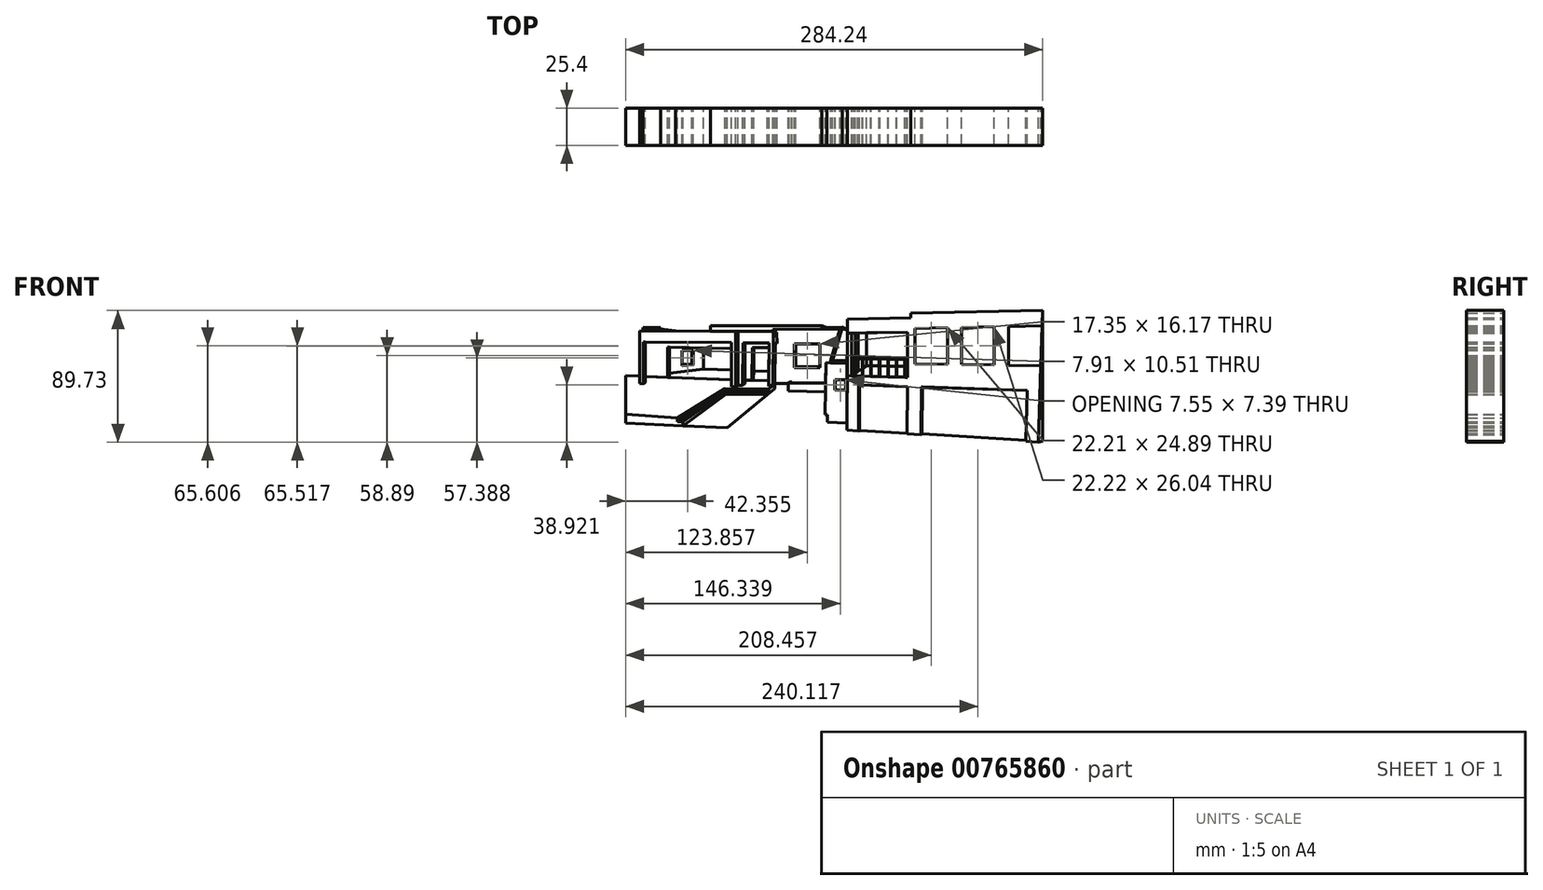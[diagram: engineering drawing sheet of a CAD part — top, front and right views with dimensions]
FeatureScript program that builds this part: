
annotation { "Feature Type Name" : "Feature", "Feature Type Description" : "" }
export const myFeature = defineFeature(function(context is Context, id is Id, definition is map)
    precondition{}
    {
        {
            var Q0;
            Q0=qCreatedBy(makeId("Front.planeOp"),FACE);
            var sketch = newSketch(context, id + "F0", { "sketchPlane" : qUnion([Q0])});
            skSolve(sketch);
        }
        {
            var Q0;
            Q0=qCreatedBy(makeId("Front.planeOp"),FACE);
            var sketch = newSketch(context, id + "F1", { "sketchPlane" : qUnion([Q0])});
            skPoint(sketch, "E0.0", {"position": v(-146.62, 105.14) * mm});
            skPoint(sketch, "E1.0", {"position": v(139.06, 105.14) * mm});
            skPoint(sketch, "E2.0", {"position": v(139.06, -109.12) * mm});
            skPoint(sketch, "E3.0", {"position": v(-146.62, -109.12) * mm});
            skLineSegment(sketch, "E4", {"start": v(-146.62, 105.14) * mm, "end": v(139.06, 105.14) * mm});
            skLineSegment(sketch, "E5", {"start": v(139.06, 105.14) * mm, "end": v(139.06, -109.12) * mm});
            skLineSegment(sketch, "E6", {"start": v(139.06, -109.12) * mm, "end": v(-146.62, -109.12) * mm});
            skLineSegment(sketch, "E7", {"start": v(-146.62, -109.12) * mm, "end": v(-146.62, 105.14) * mm});
            skLineSegment(sketch, "E8", {"start": v(-137.03, 20.59) * mm, "end": v(-48.72, 20.2) * mm});
            skLineSegment(sketch, "E9", {"start": v(-48.8, 12.25) * mm, "end": v(-49.11, -17.1) * mm});
            skLineSegment(sketch, "E10", {"start": v(-48.72, 20.2) * mm, "end": v(-45.8, 20.18) * mm});
            skLineSegment(sketch, "E11", {"start": v(-45.8, 20.18) * mm, "end": v(-43.5, 19.7) * mm});
            skLineSegment(sketch, "E12", {"start": v(-45.8, 20.18) * mm, "end": v(-46.2, -17.22) * mm});
            skLineSegment(sketch, "E13", {"start": v(-43.5, 19.7) * mm, "end": v(-43.41, 12.03) * mm});
            skLineSegment(sketch, "E14", {"start": v(-43.41, 12.03) * mm, "end": v(-44.68, 12.04) * mm});
            skLineSegment(sketch, "E15", {"start": v(-44.68, 12.04) * mm, "end": v(-44.98, -16.42) * mm});
            skLineSegment(sketch, "E16", {"start": v(-44.98, -16.42) * mm, "end": v(-46.2, -17.22) * mm});
            skLineSegment(sketch, "E17", {"start": v(-49.11, -17.1) * mm, "end": v(-46.2, -17.22) * mm});
            skLineSegment(sketch, "E18", {"start": v(-137.03, 20.59) * mm, "end": v(-137.03, -15.42) * mm});
            skLineSegment(sketch, "E19", {"start": v(-134.46, 13.05) * mm, "end": v(-74.47, 12.64) * mm});
            skLineSegment(sketch, "E20", {"start": v(-74.47, 12.64) * mm, "end": v(-74.59, -17.7) * mm});
            skLineSegment(sketch, "E21", {"start": v(-74.59, -17.7) * mm, "end": v(-71.72, -17.7) * mm});
            skLineSegment(sketch, "E22", {"start": v(-48.8, 12.25) * mm, "end": v(-66.56, 12.44) * mm});
            skLineSegment(sketch, "E23", {"start": v(-66.56, 12.44) * mm, "end": v(-66.86, -16.48) * mm});
            skLineSegment(sketch, "E24", {"start": v(-65.22, 12.42) * mm, "end": v(-65.22, -15.22) * mm});
            skLineSegment(sketch, "E25", {"start": v(-71.72, -17.7) * mm, "end": v(-70.05, -16.47) * mm});
            skLineSegment(sketch, "E26", {"start": v(-70.05, -16.47) * mm, "end": v(-66.86, -16.48) * mm});
            skLineSegment(sketch, "E27", {"start": v(-66.86, -16.48) * mm, "end": v(-65.22, -15.22) * mm});
            skLineSegment(sketch, "E28", {"start": v(-70.05, -16.47) * mm, "end": v(-70.05, 20.29) * mm});
            skLineSegment(sketch, "E29", {"start": v(-71.72, -17.7) * mm, "end": v(-71.72, 20.3) * mm});
            skLineSegment(sketch, "E30", {"start": v(-134.46, 13.05) * mm, "end": v(-134.46, -15.51) * mm});
            skLineSegment(sketch, "E31", {"start": v(-117.92, 9.32) * mm, "end": v(-74.49, 8.64) * mm});
            skLineSegment(sketch, "E32", {"start": v(-117.92, 9.32) * mm, "end": v(-117.92, -11.06) * mm});
            skLineSegment(sketch, "E33", {"start": v(-116.53, 9.3) * mm, "end": v(-116.53, -11.1) * mm});
            skLineSegment(sketch, "E34", {"start": v(-74.57, -12.64) * mm, "end": v(-133.04, -10.5) * mm});
            skLineSegment(sketch, "E35", {"start": v(-60.15, 9.2) * mm, "end": v(-48.84, 9.08) * mm});
            skLineSegment(sketch, "E36", {"start": v(-60.15, 9.2) * mm, "end": v(-60.38, -13.22) * mm});
            skLineSegment(sketch, "E37", {"start": v(-60.38, -13.22) * mm, "end": v(-59.39, -12.35) * mm});
            skLineSegment(sketch, "E38", {"start": v(-59.39, -12.35) * mm, "end": v(-59.16, 9.2) * mm});
            skLineSegment(sketch, "E39", {"start": v(-60.38, -13.22) * mm, "end": v(-65.22, -13.17) * mm});
            skLineSegment(sketch, "E40", {"start": v(-134.8, 20.58) * mm, "end": v(-134.8, 22.9) * mm});
            skLineSegment(sketch, "E41", {"start": v(-134.8, 22.9) * mm, "end": v(-122.83, 22.9) * mm});
            skLineSegment(sketch, "E42", {"start": v(-122.83, 22.9) * mm, "end": v(-122.83, 20.52) * mm});
            skLineSegment(sketch, "E43", {"start": v(-122.83, 21.71) * mm, "end": v(-112.4, 20.48) * mm});
            skLineSegment(sketch, "E44", {"start": v(-88.8, 20.37) * mm, "end": v(-88.79, 24.1) * mm});
            skLineSegment(sketch, "E45", {"start": v(-88.79, 24.1) * mm, "end": v(-12.82, 24.1) * mm});
            skLineSegment(sketch, "E46", {"start": v(-12.82, 24.1) * mm, "end": v(-12.82, 21.75) * mm});
            skLineSegment(sketch, "E47", {"start": v(-12.82, 24.1) * mm, "end": v(-9.44, 22.83) * mm});
            skLineSegment(sketch, "E48", {"start": v(-9.44, 22.83) * mm, "end": v(1.15, 22.94) * mm});
            skLineSegment(sketch, "E49", {"start": v(1.15, 22.94) * mm, "end": v(4.61, 21.65) * mm});
            skLineSegment(sketch, "E50", {"start": v(-46.06, 20.18) * mm, "end": v(-46.08, 21.6) * mm});
            skLineSegment(sketch, "E51", {"start": v(-46.08, 21.6) * mm, "end": v(0.68, 21.82) * mm});
            skLineSegment(sketch, "E52", {"start": v(0.68, 21.82) * mm, "end": v(4.6, 21.08) * mm});
            skLineSegment(sketch, "E53", {"start": v(4.65, 28.4) * mm, "end": v(4.27, -47.14) * mm});
            skLineSegment(sketch, "E54", {"start": v(4.65, 28.4) * mm, "end": v(47.74, 29.39) * mm});
            skLineSegment(sketch, "E55", {"start": v(137.62, 34.42) * mm, "end": v(47.67, 32.53) * mm});
            skLineSegment(sketch, "E56", {"start": v(47.74, 29.39) * mm, "end": v(47.67, 32.53) * mm});
            skLineSegment(sketch, "E57", {"start": v(137.62, 34.42) * mm, "end": v(134.95, -55.31) * mm});
            skLineSegment(sketch, "E58.bottom", {"start": v(-31.44, 11.66) * mm, "end": v(-14.09, 11.66) * mm});
            skLineSegment(sketch, "E58.top", {"start": v(-31.44, -4.5) * mm, "end": v(-14.09, -4.5) * mm});
            skLineSegment(sketch, "E58.left", {"start": v(-31.44, 11.66) * mm, "end": v(-31.44, -4.5) * mm});
            skLineSegment(sketch, "E58.right", {"start": v(-14.09, 11.66) * mm, "end": v(-14.09, -4.5) * mm});
            skLineSegment(sketch, "E59", {"start": v(-30.69, 11.66) * mm, "end": v(-30.69, -3.64) * mm});
            skLineSegment(sketch, "E60", {"start": v(-30.69, -3.64) * mm, "end": v(-14.09, -3.89) * mm});
            skLineSegment(sketch, "E61", {"start": v(-31.44, -4.5) * mm, "end": v(-30.69, -3.64) * mm});
            skLineSegment(sketch, "E62", {"start": v(7.63, -10.17) * mm, "end": v(45.5, -11.08) * mm});
            skLineSegment(sketch, "E63", {"start": v(45.5, -11.08) * mm, "end": v(45.65, 19.49) * mm});
            skLineSegment(sketch, "E64", {"start": v(45.65, 19.49) * mm, "end": v(4.6, 18.99) * mm});
            skLineSegment(sketch, "E65", {"start": v(7.63, -10.17) * mm, "end": v(7.63, 19.02) * mm});
            skLineSegment(sketch, "E66", {"start": v(7.63, -10.17) * mm, "end": v(4.45, -10.1) * mm});
            skLineSegment(sketch, "E67", {"start": v(-9.44, 22.83) * mm, "end": v(-9.43, 21.77) * mm});
            skLineSegment(sketch, "E68", {"start": v(1.15, 22.94) * mm, "end": v(1.17, 21.73) * mm});
            skLineSegment(sketch, "E69", {"start": v(0.68, 21.82) * mm, "end": v(0.57, -1.36) * mm});
            skLineSegment(sketch, "E70", {"start": v(-134.46, -15.51) * mm, "end": v(-137.03, -15.42) * mm});
            skLineSegment(sketch, "E71", {"start": v(-134.46, -15.51) * mm, "end": v(-133.04, -14.77) * mm});
            skLineSegment(sketch, "E72", {"start": v(50.73, 22.19) * mm, "end": v(72.94, 22.65) * mm});
            skLineSegment(sketch, "E73", {"start": v(136.5, -3.21) * mm, "end": v(114.66, -2.88) * mm});
            skLineSegment(sketch, "E74", {"start": v(50.73, -1.9) * mm, "end": v(50.73, 22.19) * mm});
            skLineSegment(sketch, "E75", {"start": v(72.94, 22.65) * mm, "end": v(72.94, -2.24) * mm});
            skLineSegment(sketch, "E76", {"start": v(82.38, 22.85) * mm, "end": v(82.38, -2.38) * mm});
            skLineSegment(sketch, "E77", {"start": v(104.6, -2.72) * mm, "end": v(104.6, 23.32) * mm});
            skLineSegment(sketch, "E78", {"start": v(114.66, 23.53) * mm, "end": v(114.66, -2.88) * mm});
            skPoint(sketch, "E79.start.orphan", {"position": v(50.73, 10.14) * mm});
            skLineSegment(sketch, "E80.trimOffspring", {"start": v(82.38, 22.85) * mm, "end": v(104.6, 23.32) * mm});
            skLineSegment(sketch, "E81.trimOffspring", {"start": v(72.94, -2.24) * mm, "end": v(50.73, -1.9) * mm});
            skPoint(sketch, "E82.end.orphan", {"position": v(104.6, 9.69) * mm});
            skPoint(sketch, "E82.start.orphan", {"position": v(82.38, 9.69) * mm});
            skLineSegment(sketch, "E83.trimOffspring", {"start": v(114.66, 23.53) * mm, "end": v(137.3, 24) * mm});
            skPoint(sketch, "E84.start.orphan", {"position": v(114.66, 9.69) * mm});
            skLineSegment(sketch, "E85.trimOffspring", {"start": v(104.6, -2.72) * mm, "end": v(82.38, -2.38) * mm});
            skLineSegment(sketch, "E86", {"start": v(12.4, -16.35) * mm, "end": v(45.5, -17.4) * mm});
            skLineSegment(sketch, "E87", {"start": v(127.33, -20) * mm, "end": v(126.3, -54.77) * mm});
            skLineSegment(sketch, "E88", {"start": v(12.4, -16.35) * mm, "end": v(12.23, -47.64) * mm});
            skLineSegment(sketch, "E89", {"start": v(4.27, -47.14) * mm, "end": v(12.23, -47.64) * mm});
            skLineSegment(sketch, "E90", {"start": v(45.5, -17.4) * mm, "end": v(45.34, -49.7) * mm});
            skLineSegment(sketch, "E91", {"start": v(55.1, -17.7) * mm, "end": v(54.94, -50.31) * mm});
            skLineSegment(sketch, "E92.trimOffspring", {"start": v(55.1, -17.7) * mm, "end": v(127.33, -20) * mm});
            skLineSegment(sketch, "E93", {"start": v(7.63, 2.73) * mm, "end": v(45.57, 2.17) * mm});
            skLineSegment(sketch, "E94", {"start": v(7.63, 1.7) * mm, "end": v(45.56, 1.13) * mm});
            skLineSegment(sketch, "E95", {"start": v(8.88, 1.68) * mm, "end": v(8.88, -10.2) * mm});
            skLineSegment(sketch, "E96", {"start": v(9.36, 1.67) * mm, "end": v(9.36, -10.2) * mm});
            skLineSegment(sketch, "E97.1.0.0", {"start": v(15.16, 1.57) * mm, "end": v(15.16, -10.31) * mm});
            skLineSegment(sketch, "E97.1.0.1", {"start": v(14.69, 1.57) * mm, "end": v(14.69, -10.3) * mm});
            skLineSegment(sketch, "E97.2.0.0", {"start": v(20.97, 1.46) * mm, "end": v(20.97, -10.42) * mm});
            skLineSegment(sketch, "E97.2.0.1", {"start": v(20.49, 1.47) * mm, "end": v(20.49, -10.4) * mm});
            skLineSegment(sketch, "E97.3.0.0", {"start": v(26.77, 1.36) * mm, "end": v(26.77, -10.52) * mm});
            skLineSegment(sketch, "E97.3.0.1", {"start": v(26.29, 1.37) * mm, "end": v(26.29, -10.5) * mm});
            skLineSegment(sketch, "E97.4.0.0", {"start": v(32.57, 1.26) * mm, "end": v(32.57, -10.62) * mm});
            skLineSegment(sketch, "E97.4.0.1", {"start": v(32.1, 1.26) * mm, "end": v(32.1, -10.61) * mm});
            skLineSegment(sketch, "E97.5.0.0", {"start": v(38.37, 1.15) * mm, "end": v(38.37, -10.73) * mm});
            skLineSegment(sketch, "E97.5.0.1", {"start": v(37.9, 1.16) * mm, "end": v(37.9, -10.71) * mm});
            skLineSegment(sketch, "E97.6.0.0", {"start": v(44.17, 1.05) * mm, "end": v(44.17, -10.83) * mm});
            skLineSegment(sketch, "E97.6.0.1", {"start": v(43.7, 1.06) * mm, "end": v(43.7, -10.82) * mm});
            skLineSegment(sketch, "E97.direction1", {"start": v(9.36, -10.2) * mm, "end": v(15.16, -10.31) * mm, "construction": true});
            skLineSegment(sketch, "E98", {"start": v(14.69, 1.57) * mm, "end": v(14.69, 1.6) * mm});
            skLineSegment(sketch, "E99", {"start": v(15.16, 1.57) * mm, "end": v(15.16, 1.58) * mm});
            skLineSegment(sketch, "E100", {"start": v(20.49, 1.47) * mm, "end": v(20.49, 1.5) * mm});
            skLineSegment(sketch, "E101", {"start": v(20.97, 1.46) * mm, "end": v(20.97, 1.5) * mm});
            skLineSegment(sketch, "E102", {"start": v(26.29, 1.37) * mm, "end": v(26.29, 1.42) * mm});
            skLineSegment(sketch, "E103", {"start": v(26.77, 1.36) * mm, "end": v(26.77, 1.41) * mm});
            skLineSegment(sketch, "E104", {"start": v(32.1, 1.26) * mm, "end": v(32.1, 1.33) * mm});
            skLineSegment(sketch, "E105", {"start": v(32.57, 1.26) * mm, "end": v(32.57, 1.33) * mm});
            skLineSegment(sketch, "E106", {"start": v(37.9, 1.16) * mm, "end": v(37.9, 1.25) * mm});
            skLineSegment(sketch, "E107", {"start": v(38.37, 1.15) * mm, "end": v(38.37, 1.24) * mm});
            skLineSegment(sketch, "E108", {"start": v(44.17, 1.05) * mm, "end": v(44.17, 1.15) * mm});
            skLineSegment(sketch, "E109", {"start": v(43.7, 1.06) * mm, "end": v(43.7, 1.16) * mm});
            skLineSegment(sketch, "E110", {"start": v(44.17, -10.83) * mm, "end": v(44.17, -11.05) * mm});
            skLineSegment(sketch, "E111", {"start": v(43.7, -10.82) * mm, "end": v(43.7, -11.04) * mm});
            skLineSegment(sketch, "E112", {"start": v(37.9, -10.71) * mm, "end": v(37.9, -10.9) * mm});
            skLineSegment(sketch, "E113", {"start": v(38.37, -10.73) * mm, "end": v(38.37, -10.91) * mm});
            skLineSegment(sketch, "E114", {"start": v(32.1, -10.61) * mm, "end": v(32.1, -10.76) * mm});
            skLineSegment(sketch, "E115", {"start": v(32.57, -10.62) * mm, "end": v(32.57, -10.77) * mm});
            skLineSegment(sketch, "E116", {"start": v(26.29, -10.5) * mm, "end": v(26.29, -10.62) * mm});
            skLineSegment(sketch, "E117", {"start": v(26.77, -10.52) * mm, "end": v(26.77, -10.63) * mm});
            skLineSegment(sketch, "E118", {"start": v(20.49, -10.4) * mm, "end": v(20.49, -10.48) * mm});
            skLineSegment(sketch, "E119", {"start": v(20.97, -10.42) * mm, "end": v(20.97, -10.49) * mm});
            skLineSegment(sketch, "E120", {"start": v(14.69, -10.3) * mm, "end": v(14.69, -10.34) * mm});
            skLineSegment(sketch, "E121", {"start": v(15.16, -10.31) * mm, "end": v(15.16, -10.35) * mm});
            skLineSegment(sketch, "E122", {"start": v(12.23, -47.64) * mm, "end": v(12.73, -47.24) * mm});
            skLineSegment(sketch, "E123", {"start": v(12.73, -47.24) * mm, "end": v(12.88, -16.37) * mm});
            skLineSegment(sketch, "E124", {"start": v(54.94, -50.31) * mm, "end": v(55.52, -49.75) * mm});
            skLineSegment(sketch, "E125", {"start": v(55.52, -49.75) * mm, "end": v(55.64, -17.73) * mm});
            skLineSegment(sketch, "E126", {"start": v(12.73, -47.24) * mm, "end": v(45.34, -49.28) * mm});
            skLineSegment(sketch, "E127", {"start": v(55.52, -49.75) * mm, "end": v(126.32, -54.18) * mm});
            skLineSegment(sketch, "E128.trimOffspring", {"start": v(126.3, -54.77) * mm, "end": v(134.95, -55.31) * mm});
            skLineSegment(sketch, "E129.trimOffspring", {"start": v(45.34, -49.7) * mm, "end": v(54.94, -50.31) * mm});
            skLineSegment(sketch, "E130", {"start": v(-9.08, -41.6) * mm, "end": v(-9.08, -36.6) * mm});
            skLineSegment(sketch, "E131", {"start": v(-9.08, -36.6) * mm, "end": v(-10.58, -36.6) * mm});
            skLineSegment(sketch, "E132", {"start": v(-10.58, -36.6) * mm, "end": v(-9.86, -1.14) * mm});
            skLineSegment(sketch, "E133", {"start": v(-9.86, -1.14) * mm, "end": v(4.5, -1.44) * mm});
            skLineSegment(sketch, "E134", {"start": v(-4.06, -19.93) * mm, "end": v(-3.9, -12.7) * mm});
            skLineSegment(sketch, "E135", {"start": v(-3.9, -12.7) * mm, "end": v(3.5, -12.85) * mm});
            skLineSegment(sketch, "E136", {"start": v(3.5, -12.85) * mm, "end": v(3.34, -19.93) * mm});
            skLineSegment(sketch, "E137", {"start": v(-4.06, -19.93) * mm, "end": v(3.34, -20.08) * mm});
            skLineSegment(sketch, "E138", {"start": v(3.34, -19.93) * mm, "end": v(3.34, -20.08) * mm});
            skLineSegment(sketch, "E139", {"start": v(-9.08, -41.6) * mm, "end": v(4.3, -42.2) * mm});
            skLineSegment(sketch, "E140", {"start": v(-35.55, -15.05) * mm, "end": v(-10.14, -15.18) * mm});
            skLineSegment(sketch, "E141", {"start": v(-35.55, -15.05) * mm, "end": v(-35.03, -14.37) * mm});
            skLineSegment(sketch, "E142", {"start": v(-33.16, -14.37) * mm, "end": v(-33.57, -14.9) * mm});
            skLineSegment(sketch, "E143", {"start": v(-35.55, -15.05) * mm, "end": v(-35.55, -20.4) * mm});
            skLineSegment(sketch, "E144", {"start": v(-35.55, -20.4) * mm, "end": v(-10.26, -20.9) * mm});
            skLineSegment(sketch, "E145", {"start": v(-44.97, -15.39) * mm, "end": v(-35.55, -15.49) * mm});
            skLineSegment(sketch, "E146", {"start": v(-35.03, -14.37) * mm, "end": v(-33.16, -14.37) * mm});
            skLineSegment(sketch, "E147", {"start": v(-33.57, -14.9) * mm, "end": v(-10.14, -15.02) * mm});
            skLineSegment(sketch, "E148.trimOffspring", {"start": v(15.15, -47.4) * mm, "end": v(15.15, -47.65) * mm});
            skLineSegment(sketch, "E149", {"start": v(-100.3, 7.33) * mm, "end": v(-100.3, -2.64) * mm});
            skLineSegment(sketch, "E150", {"start": v(-100.3, -2.64) * mm, "end": v(-108.22, -3.18) * mm});
            skLineSegment(sketch, "E151", {"start": v(-108.22, -3.18) * mm, "end": v(-108.06, 7.33) * mm});
            skLineSegment(sketch, "E152", {"start": v(-108.06, 7.33) * mm, "end": v(-100.3, 7.33) * mm});
            skLineSegment(sketch, "E153", {"start": v(-101.46, 7.33) * mm, "end": v(-101.46, -2) * mm});
            skLineSegment(sketch, "E154", {"start": v(-101.46, -2) * mm, "end": v(-108.21, -2.47) * mm});
            skLineSegment(sketch, "E155", {"start": v(-101.46, -2) * mm, "end": v(-100.3, -2.64) * mm});
            skLineSegment(sketch, "E156", {"start": v(-116.53, -8.37) * mm, "end": v(-93.36, -5.38) * mm});
            skLineSegment(sketch, "E157", {"start": v(-93.36, -5.38) * mm, "end": v(-93.36, 8.94) * mm});
            skLineSegment(sketch, "E158", {"start": v(-60.38, -13.22) * mm, "end": v(-49.07, -13.33) * mm});
            skLineSegment(sketch, "E159", {"start": v(-133.04, -14.77) * mm, "end": v(-133.04, 13.04) * mm});
            skLineSegment(sketch, "E160", {"start": v(7.63, -1.52) * mm, "end": v(8.88, -1.29) * mm});
            skLineSegment(sketch, "E161", {"start": v(9.9, 19.05) * mm, "end": v(9.9, 3.6) * mm});
            skLineSegment(sketch, "E162", {"start": v(9.9, -7.3) * mm, "end": v(11.96, -7.32) * mm});
            skLineSegment(sketch, "E163", {"start": v(11.96, -7.32) * mm, "end": v(11.96, 1.63) * mm});
            skLineSegment(sketch, "E164.trimOffspring", {"start": v(9.36, -1.2) * mm, "end": v(9.9, -1.1) * mm});
            skLineSegment(sketch, "E165", {"start": v(7.63, -10.17) * mm, "end": v(8.88, -9.3) * mm});
            skLineSegment(sketch, "E166", {"start": v(17.64, -3.23) * mm, "end": v(17.64, 1.55) * mm});
            skLineSegment(sketch, "E167", {"start": v(17.64, -3.23) * mm, "end": v(20.49, -3.27) * mm});
            skLineSegment(sketch, "E168", {"start": v(7.63, -8.47) * mm, "end": v(8.88, -7.82) * mm});
            skLineSegment(sketch, "E169.trimOffspring", {"start": v(9.36, -7.58) * mm, "end": v(9.9, -7.3) * mm});
            skLineSegment(sketch, "E170.trimOffspring", {"start": v(9.36, -8.97) * mm, "end": v(11.74, -7.32) * mm});
            skLineSegment(sketch, "E171.trimOffspring", {"start": v(11.96, -7.17) * mm, "end": v(14.69, -5.28) * mm});
            skLineSegment(sketch, "E172.trimOffspring", {"start": v(15.16, -4.95) * mm, "end": v(17.64, -3.23) * mm});
            skLineSegment(sketch, "E173.trimOffspring", {"start": v(17.64, 2.58) * mm, "end": v(17.64, 19.14) * mm});
            skLineSegment(sketch, "E174.trimOffspring", {"start": v(9.9, 1.66) * mm, "end": v(9.9, -7.3) * mm});
            skLineSegment(sketch, "E175.trimOffspring", {"start": v(11.96, 2.67) * mm, "end": v(11.96, 19.08) * mm});
            skLineSegment(sketch, "E176", {"start": v(-6.8, -1.2) * mm, "end": v(-6.8, 0.37) * mm});
            skLineSegment(sketch, "E177", {"start": v(-6.8, 0.37) * mm, "end": v(4.5, 0.14) * mm});
            skLineSegment(sketch, "E178", {"start": v(-6.8, 0.37) * mm, "end": v(-0.32, 21.81) * mm});
            skLineSegment(sketch, "E179", {"start": v(0.68, 21.82) * mm, "end": v(-5.54, 0.34) * mm});
            skLineSegment(sketch, "E180", {"start": v(7.63, 0.14) * mm, "end": v(8.88, 0.11) * mm});
            skLineSegment(sketch, "E181.trimOffspring", {"start": v(9.36, 0.1) * mm, "end": v(9.9, 0.1) * mm});
            skLineSegment(sketch, "E182.trimOffspring", {"start": v(20.97, -3.28) * mm, "end": v(26.29, -3.36) * mm});
            skLineSegment(sketch, "E183.trimOffspring", {"start": v(26.77, -3.37) * mm, "end": v(32.1, -3.44) * mm});
            skLineSegment(sketch, "E184.trimOffspring", {"start": v(32.57, -3.45) * mm, "end": v(37.9, -3.53) * mm});
            skLineSegment(sketch, "E185.trimOffspring", {"start": v(38.37, -3.54) * mm, "end": v(43.7, -3.62) * mm});
            skLineSegment(sketch, "E186.trimOffspring", {"start": v(44.17, -3.62) * mm, "end": v(45.54, -3.64) * mm});
            skLineSegment(sketch, "E187", {"start": v(-3.6, -12.7) * mm, "end": v(-3.74, -19.7) * mm});
            skLineSegment(sketch, "E188", {"start": v(-3.74, -19.7) * mm, "end": v(3.35, -19.87) * mm});
            skLineSegment(sketch, "E189", {"start": v(-4.06, -19.93) * mm, "end": v(-3.74, -19.7) * mm});
            skLineSegment(sketch, "E190", {"start": v(7.63, 2.73) * mm, "end": v(11.96, 3.6) * mm});
            skLineSegment(sketch, "E191", {"start": v(11.96, 3.6) * mm, "end": v(9.9, 3.6) * mm});
            skLineSegment(sketch, "E192", {"start": v(9.9, 3.6) * mm, "end": v(7.63, 3.15) * mm});
            skLineSegment(sketch, "E193.trimOffspring", {"start": v(9.9, 2.88) * mm, "end": v(9.9, 2.7) * mm});
            skLineSegment(sketch, "E194", {"start": v(11.96, 3.6) * mm, "end": v(11.96, 3.3) * mm});
            skLineSegment(sketch, "E195", {"start": v(11.96, 3.3) * mm, "end": v(9.07, 2.71) * mm});
            skLineSegment(sketch, "E196", {"start": v(-93.36, -5.38) * mm, "end": v(-74.54, -6.07) * mm});
            skLineSegment(sketch, "E197.trimOffspring", {"start": v(-59.33, -6.62) * mm, "end": v(-49, -7) * mm});
            skLineSegment(sketch, "E198", {"start": v(137.62, 34.42) * mm, "end": v(137.62, -54.63) * mm});
            skLineSegment(sketch, "E199", {"start": v(134.95, -55.31) * mm, "end": v(137.62, -54.63) * mm});
            skLineSegment(sketch, "E200", {"start": v(137.62, -54.63) * mm, "end": v(139.06, -54.72) * mm});
            skSolve(sketch);
        }
        {
            var Q0;
            {var subQ7=sQuery(id+"F1.wireOp",EDGE,"E44");Q0=makeQuery(id+"F1.imprint","IMPRINT",FACE,{"disambiguationData":[TD([[makeQuery(id+"F1.imprint","IMPRINT",EDGE,{"derivedFrom":subQ7}),-1.0]])]});}
            extrude(context, id + "F2", {"entities" : qUnion([Q0]), "depth" : 25.4 * mm, "offsetDistance" : 25.4 * mm});
        }
        {
            var Q0;
            {var subQ0=sQuery(id+"F1.wireOp",EDGE,"E46");Q0=makeQuery(id+"F1.imprint","IMPRINT",FACE,{"disambiguationData":[TD([[makeQuery(id+"F1.imprint","IMPRINT",EDGE,{"derivedFrom":subQ0}),1.0]])]});}
            extrude(context, id + "F3", {"entities" : qUnion([Q0]), "depth" : 25.4 * mm, "offsetDistance" : 25.4 * mm});
        }
        {
            var Q0;
            Q0=makeQuery(id+"F1.imprint","IMPRINT",FACE,{"disambiguationData":[TD([[makeQuery(id+"F1.imprint","IMPRINT",EDGE,{"derivedFrom":sQuery(id+"F1.wireOp",EDGE,"E48")}),-1.0]])]});
            extrude(context, id + "F4", {"entities" : qUnion([Q0]), "depth" : 25.4 * mm, "offsetDistance" : 25.4 * mm});
        }
        {
            var Q0;
            {var subQ0=sQuery(id+"F1.wireOp",EDGE,"E49");Q0=makeQuery(id+"F1.imprint","IMPRINT",FACE,{"disambiguationData":[TD([[makeQuery(id+"F1.imprint","IMPRINT",EDGE,{"derivedFrom":subQ0}),-1.0]])]});}
            extrude(context, id + "F5", {"entities" : qUnion([Q0]), "depth" : 25.4 * mm, "offsetDistance" : 25.4 * mm});
        }
        {
            var Q0;
            {var subQ1=sQuery(id+"F1.wireOp",EDGE,"E40");Q0=makeQuery(id+"F1.imprint","IMPRINT",FACE,{"disambiguationData":[TD([[makeQuery(id+"F1.imprint","IMPRINT",EDGE,{"derivedFrom":subQ1}),-1.0]])]});}
            extrude(context, id + "F6", {"entities" : qUnion([Q0]), "depth" : 25.4 * mm, "offsetDistance" : 25.4 * mm});
        }
        {
            var Q0;
            {var subQ3=sQuery(id+"F1.wireOp",EDGE,"E43");Q0=makeQuery(id+"F1.imprint","IMPRINT",FACE,{"disambiguationData":[TD([[makeQuery(id+"F1.imprint","IMPRINT",EDGE,{"derivedFrom":subQ3}),-1.0]])]});}
            extrude(context, id + "F7", {"entities" : qUnion([Q0]), "depth" : 25.4 * mm, "offsetDistance" : 25.4 * mm});
        }
        {
            var Q0;
            {var subQ3=sQuery(id+"F1.wireOp",EDGE,"E32");Q0=makeQuery(id+"F1.imprint","IMPRINT",FACE,{"disambiguationData":[TD([[makeQuery(id+"F1.imprint","IMPRINT",EDGE,{"derivedFrom":subQ3}),-1.0]])]});}
            var Q1;
            {var subQ4=sQuery(id+"F1.wireOp",EDGE,"E36");Q1=makeQuery(id+"F1.imprint","IMPRINT",FACE,{"disambiguationData":[TD([[makeQuery(id+"F1.imprint","IMPRINT",EDGE,{"derivedFrom":subQ4}),-1.0]])]});}
            var Q2;
            {var subQ14=sQuery(id+"F1.wireOp",EDGE,"E11");Q2=makeQuery(id+"F1.imprint","IMPRINT",FACE,{"disambiguationData":[TD([[makeQuery(id+"F1.imprint","IMPRINT",EDGE,{"derivedFrom":subQ14}),1.0]])]});}
            extrude(context, id + "F8", {"entities" : qUnion([Q0, Q1, Q2]), "depth" : 25.4 * mm, "offsetDistance" : 25.4 * mm});
        }
        {
            var Q0;
            {var subQ3=sQuery(id+"F1.wireOp",EDGE,"E18");Q0=makeQuery(id+"F1.imprint","IMPRINT",FACE,{"disambiguationData":[TD([[makeQuery(id+"F1.imprint","IMPRINT",EDGE,{"derivedFrom":subQ3}),1.0]])]});}
            var Q1;
            {var subQ0=sQuery(id+"F1.wireOp",EDGE,"E12");Q1=makeQuery(id+"F1.imprint","IMPRINT",FACE,{"disambiguationData":[TD([[makeQuery(id+"F1.imprint","IMPRINT",EDGE,{"derivedFrom":subQ0}),-1.0]])]});}
            var Q2;
            Q2=makeQuery(id+"F1.imprint","IMPRINT",FACE,{"disambiguationData":[TD([[makeQuery(id+"F1.imprint","IMPRINT",EDGE,{"derivedFrom":sQuery(id+"F1.wireOp",EDGE,"E130")}),-1.0]])]});
            extrude(context, id + "F9", {"entities" : qUnion([Q0, Q1, Q2]), "depth" : 25.4 * mm, "offsetDistance" : 25.4 * mm});
        }
        {
            var Q0;
            {var subQ24=sQuery(id+"F1.wireOp",EDGE,"E54");Q0=makeQuery(id+"F1.imprint","IMPRINT",FACE,{"disambiguationData":[TD([[makeQuery(id+"F1.imprint","IMPRINT",EDGE,{"derivedFrom":subQ24}),-1.0]])]});}
            extrude(context, id + "F10", {"entities" : qUnion([Q0]), "depth" : 25.4 * mm, "offsetDistance" : 25.4 * mm});
        }
        {
            var Q0;
            {var subQ4=sQuery(id+"F1.wireOp",EDGE,"E125");Q0=makeQuery(id+"F1.imprint","IMPRINT",FACE,{"disambiguationData":[TD([[makeQuery(id+"F1.imprint","IMPRINT",EDGE,{"derivedFrom":subQ4}),-1.0]])]});}
            var Q1;
            {var subQ1=sQuery(id+"F1.wireOp",EDGE,"E123");Q1=makeQuery(id+"F1.imprint","IMPRINT",FACE,{"disambiguationData":[TD([[makeQuery(id+"F1.imprint","IMPRINT",EDGE,{"derivedFrom":subQ1}),-1.0]])]});}
            extrude(context, id + "F11", {"entities" : qUnion([Q0, Q1]), "depth" : 25.4 * mm, "offsetDistance" : 25.4 * mm});
        }
        {
            var Q0;
            {var subQ4=sQuery(id+"F1.wireOp",EDGE,"E153");Q0=makeQuery(id+"F1.imprint","IMPRINT",FACE,{"disambiguationData":[TD([[makeQuery(id+"F1.imprint","IMPRINT",EDGE,{"derivedFrom":subQ4}),-1.0]])]});}
            var Q1;
            {var subQ3=sQuery(id+"F1.wireOp",EDGE,"E187");Q1=makeQuery(id+"F1.imprint","IMPRINT",FACE,{"disambiguationData":[TD([[makeQuery(id+"F1.imprint","IMPRINT",EDGE,{"derivedFrom":subQ3}),1.0]])]});}
            var Q2;
            {var subQ3=sQuery(id+"F1.wireOp",EDGE,"E59");Q2=makeQuery(id+"F1.imprint","IMPRINT",FACE,{"disambiguationData":[TD([[makeQuery(id+"F1.imprint","IMPRINT",EDGE,{"derivedFrom":subQ3}),1.0]])]});}
            var Q3;
            Q3=makeQuery(id+"F1.imprint","IMPRINT",FACE,{"disambiguationData":[TD([[makeQuery(id+"F1.imprint","IMPRINT",EDGE,{"derivedFrom":sQuery(id+"F1.wireOp",EDGE,"E72")}),-1.0]])]});
            var Q4;
            Q4=makeQuery(id+"F1.imprint","IMPRINT",FACE,{"disambiguationData":[TD([[makeQuery(id+"F1.imprint","IMPRINT",EDGE,{"derivedFrom":sQuery(id+"F1.wireOp",EDGE,"E76")}),1.0]])]});
            var Q5;
            {var subQ0=sQuery(id+"F1.wireOp",EDGE,"E73");Q5=makeQuery(id+"F1.imprint","IMPRINT",FACE,{"disambiguationData":[TD([[makeQuery(id+"F1.imprint","IMPRINT",EDGE,{"derivedFrom":subQ0}),-1.0]])]});}
            extrude(context, id + "F12", {"entities" : qUnion([Q0, Q1, Q2, Q3, Q4, Q5]), "depth" : 25.4 * mm, "offsetDistance" : 25.4 * mm});
        }
        {
            var Q0;
            {var subQ5=sQuery(id+"F1.wireOp",EDGE,"E66");Q0=makeQuery(id+"F1.imprint","IMPRINT",FACE,{"disambiguationData":[TD([[makeQuery(id+"F1.imprint","IMPRINT",EDGE,{"derivedFrom":subQ5}),-1.0]])]});}
            extrude(context, id + "F13", {"entities" : qUnion([Q0]), "depth" : 25.4 * mm, "offsetDistance" : 25.4 * mm});
        }
        {
            var Q0;
            {var subQ0=sQuery(id+"F1.wireOp",EDGE,"E161");Q0=makeQuery(id+"F1.imprint","IMPRINT",FACE,{"disambiguationData":[TD([[makeQuery(id+"F1.imprint","IMPRINT",EDGE,{"derivedFrom":subQ0}),1.0]])]});}
            var Q1;
            {var subQ0=sQuery(id+"F1.wireOp",EDGE,"E163");var subQ7=sQuery(id+"F1.wireOp",EDGE,"E94");var subQ8=makeQuery(id+"F1.imprint","INTERSECT",VERTEX,{"derivedFrom":[subQ7,subQ0]});Q1=makeQuery(id+"F1.imprint","IMPRINT",FACE,{"disambiguationData":[TD([[makeQuery(id+"F1.imprint","IMPRINT",EDGE,{"disambiguationData":[TD([[subQ8,1.0]])],"derivedFrom":subQ7}),-1.0]])]});}
            extrude(context, id + "F14", {"entities" : qUnion([Q0, Q1]), "depth" : 25.4 * mm, "offsetDistance" : 25.4 * mm});
        }
        {
            var Q0;
            {var subQ6=sQuery(id+"F1.wireOp",EDGE,"E93");var subQ21=sQuery(id+"F1.wireOp",EDGE,"E63");var subQ22=makeQuery(id+"F1.imprint","INTERSECT",VERTEX,{"derivedFrom":[subQ21,subQ6]});Q0=makeQuery(id+"F1.imprint","IMPRINT",FACE,{"disambiguationData":[TD([[makeQuery(id+"F1.imprint","IMPRINT",EDGE,{"disambiguationData":[TD([[subQ22,1.0]])],"derivedFrom":subQ21}),1.0]])]});}
            var Q1;
            {var subQ6=sQuery(id+"F1.wireOp",EDGE,"E98");Q1=makeQuery(id+"F1.imprint","IMPRINT",FACE,{"disambiguationData":[TD([[makeQuery(id+"F1.imprint","IMPRINT",EDGE,{"derivedFrom":subQ6}),-1.0]])]});}
            var Q2;
            {var subQ4=sQuery(id+"F1.wireOp",EDGE,"E95");var subQ8=sQuery(id+"F1.wireOp",EDGE,"E62");var subQ9=makeQuery(id+"F1.imprint","INTERSECT",VERTEX,{"derivedFrom":[subQ8,subQ4]});Q2=makeQuery(id+"F1.imprint","IMPRINT",FACE,{"disambiguationData":[TD([[makeQuery(id+"F1.imprint","IMPRINT",EDGE,{"disambiguationData":[TD([[subQ9,-1.0]])],"derivedFrom":subQ8}),1.0]])]});}
            var Q3;
            {var subQ4=sQuery(id+"F1.wireOp",EDGE,"E100");Q3=makeQuery(id+"F1.imprint","IMPRINT",FACE,{"disambiguationData":[TD([[makeQuery(id+"F1.imprint","IMPRINT",EDGE,{"derivedFrom":subQ4}),-1.0]])]});}
            var Q4;
            {var subQ5=sQuery(id+"F1.wireOp",EDGE,"E102");Q4=makeQuery(id+"F1.imprint","IMPRINT",FACE,{"disambiguationData":[TD([[makeQuery(id+"F1.imprint","IMPRINT",EDGE,{"derivedFrom":subQ5}),-1.0]])]});}
            var Q5;
            {var subQ3=sQuery(id+"F1.wireOp",EDGE,"E104");Q5=makeQuery(id+"F1.imprint","IMPRINT",FACE,{"disambiguationData":[TD([[makeQuery(id+"F1.imprint","IMPRINT",EDGE,{"derivedFrom":subQ3}),-1.0]])]});}
            var Q6;
            {var subQ5=sQuery(id+"F1.wireOp",EDGE,"E106");Q6=makeQuery(id+"F1.imprint","IMPRINT",FACE,{"disambiguationData":[TD([[makeQuery(id+"F1.imprint","IMPRINT",EDGE,{"derivedFrom":subQ5}),-1.0]])]});}
            var Q7;
            {var subQ3=sQuery(id+"F1.wireOp",EDGE,"E108");Q7=makeQuery(id+"F1.imprint","IMPRINT",FACE,{"disambiguationData":[TD([[makeQuery(id+"F1.imprint","IMPRINT",EDGE,{"derivedFrom":subQ3}),1.0]])]});}
            extrude(context, id + "F15", {"entities" : qUnion([Q0, Q1, Q2, Q3, Q4, Q5, Q6, Q7]), "depth" : 25.4 * mm, "offsetDistance" : 25.4 * mm});
        }
        {
            var Q0;
            {var subQ5=sQuery(id+"F1.wireOp",EDGE,"E173.trimOffspring");Q0=makeQuery(id+"F1.imprint","IMPRINT",FACE,{"disambiguationData":[TD([[makeQuery(id+"F1.imprint","IMPRINT",EDGE,{"derivedFrom":subQ5}),-1.0]])]});}
            var Q1;
            {var subQ1=sQuery(id+"F1.wireOp",EDGE,"E100");Q1=makeQuery(id+"F1.imprint","IMPRINT",FACE,{"disambiguationData":[TD([[makeQuery(id+"F1.imprint","IMPRINT",EDGE,{"derivedFrom":subQ1}),1.0]])]});}
            var Q2;
            {var subQ0=sQuery(id+"F1.wireOp",EDGE,"E101");Q2=makeQuery(id+"F1.imprint","IMPRINT",FACE,{"disambiguationData":[TD([[makeQuery(id+"F1.imprint","IMPRINT",EDGE,{"derivedFrom":subQ0}),-1.0]])]});}
            var Q3;
            {var subQ0=sQuery(id+"F1.wireOp",EDGE,"E103");Q3=makeQuery(id+"F1.imprint","IMPRINT",FACE,{"disambiguationData":[TD([[makeQuery(id+"F1.imprint","IMPRINT",EDGE,{"derivedFrom":subQ0}),-1.0]])]});}
            var Q4;
            {var subQ0=sQuery(id+"F1.wireOp",EDGE,"E105");Q4=makeQuery(id+"F1.imprint","IMPRINT",FACE,{"disambiguationData":[TD([[makeQuery(id+"F1.imprint","IMPRINT",EDGE,{"derivedFrom":subQ0}),-1.0]])]});}
            var Q5;
            {var subQ0=sQuery(id+"F1.wireOp",EDGE,"E107");Q5=makeQuery(id+"F1.imprint","IMPRINT",FACE,{"disambiguationData":[TD([[makeQuery(id+"F1.imprint","IMPRINT",EDGE,{"derivedFrom":subQ0}),-1.0]])]});}
            var Q6;
            {var subQ0=sQuery(id+"F1.wireOp",EDGE,"E108");Q6=makeQuery(id+"F1.imprint","IMPRINT",FACE,{"disambiguationData":[TD([[makeQuery(id+"F1.imprint","IMPRINT",EDGE,{"derivedFrom":subQ0}),-1.0]])]});}
            var Q7;
            {var subQ4=sQuery(id+"F1.wireOp",EDGE,"E157");Q7=makeQuery(id+"F1.imprint","IMPRINT",FACE,{"disambiguationData":[TD([[makeQuery(id+"F1.imprint","IMPRINT",EDGE,{"derivedFrom":subQ4}),-1.0]])]});}
            extrude(context, id + "F16", {"entities" : qUnion([Q0, Q1, Q2, Q3, Q4, Q5, Q6, Q7]), "depth" : 25.4 * mm, "offsetDistance" : 25.4 * mm});
        }
        {
            var Q0;
            {var subQ0=sQuery(id+"F1.wireOp",EDGE,"E173.trimOffspring");Q0=makeQuery(id+"F1.imprint","IMPRINT",FACE,{"disambiguationData":[TD([[makeQuery(id+"F1.imprint","IMPRINT",EDGE,{"derivedFrom":subQ0}),1.0]])]});}
            var Q1;
            {var subQ4=sQuery(id+"F1.wireOp",EDGE,"E98");Q1=makeQuery(id+"F1.imprint","IMPRINT",FACE,{"disambiguationData":[TD([[makeQuery(id+"F1.imprint","IMPRINT",EDGE,{"derivedFrom":subQ4}),1.0]])]});}
            var Q2;
            {var subQ1=sQuery(id+"F1.wireOp",EDGE,"E99");Q2=makeQuery(id+"F1.imprint","IMPRINT",FACE,{"disambiguationData":[TD([[makeQuery(id+"F1.imprint","IMPRINT",EDGE,{"derivedFrom":subQ1}),-1.0]])]});}
            var Q3;
            {var subQ1=sQuery(id+"F1.wireOp",EDGE,"E149");Q3=makeQuery(id+"F1.imprint","IMPRINT",FACE,{"disambiguationData":[TD([[makeQuery(id+"F1.imprint","IMPRINT",EDGE,{"derivedFrom":subQ1}),1.0]])]});}
            extrude(context, id + "F17", {"entities" : qUnion([Q0, Q1, Q2, Q3]), "depth" : 25.4 * mm, "offsetDistance" : 25.4 * mm});
        }
        {
            var Q0;
            {var subQ0=sQuery(id+"F1.wireOp",EDGE,"E120");Q0=makeQuery(id+"F1.imprint","IMPRINT",FACE,{"disambiguationData":[TD([[makeQuery(id+"F1.imprint","IMPRINT",EDGE,{"derivedFrom":subQ0}),-1.0]])]});}
            var Q1;
            {var subQ0=sQuery(id+"F1.wireOp",EDGE,"E118");Q1=makeQuery(id+"F1.imprint","IMPRINT",FACE,{"disambiguationData":[TD([[makeQuery(id+"F1.imprint","IMPRINT",EDGE,{"derivedFrom":subQ0}),-1.0]])]});}
            var Q2;
            {var subQ0=sQuery(id+"F1.wireOp",EDGE,"E116");Q2=makeQuery(id+"F1.imprint","IMPRINT",FACE,{"disambiguationData":[TD([[makeQuery(id+"F1.imprint","IMPRINT",EDGE,{"derivedFrom":subQ0}),-1.0]])]});}
            var Q3;
            {var subQ3=sQuery(id+"F1.wireOp",EDGE,"E114");Q3=makeQuery(id+"F1.imprint","IMPRINT",FACE,{"disambiguationData":[TD([[makeQuery(id+"F1.imprint","IMPRINT",EDGE,{"derivedFrom":subQ3}),-1.0]])]});}
            var Q4;
            {var subQ0=sQuery(id+"F1.wireOp",EDGE,"E112");Q4=makeQuery(id+"F1.imprint","IMPRINT",FACE,{"disambiguationData":[TD([[makeQuery(id+"F1.imprint","IMPRINT",EDGE,{"derivedFrom":subQ0}),-1.0]])]});}
            var Q5;
            {var subQ0=sQuery(id+"F1.wireOp",EDGE,"E111");Q5=makeQuery(id+"F1.imprint","IMPRINT",FACE,{"disambiguationData":[TD([[makeQuery(id+"F1.imprint","IMPRINT",EDGE,{"derivedFrom":subQ0}),-1.0]])]});}
            var Q6;
            {var subQ4=sQuery(id+"F1.wireOp",EDGE,"E110");Q6=makeQuery(id+"F1.imprint","IMPRINT",FACE,{"disambiguationData":[TD([[makeQuery(id+"F1.imprint","IMPRINT",EDGE,{"derivedFrom":subQ4}),1.0]])]});}
            extrude(context, id + "F18", {"entities" : qUnion([Q0, Q1, Q2, Q3, Q4, Q5, Q6]), "depth" : 25.4 * mm, "offsetDistance" : 25.4 * mm});
        }
        {
            var Q0;
            {var subQ3=sQuery(id+"F1.wireOp",EDGE,"E197.trimOffspring");Q0=makeQuery(id+"F1.imprint","IMPRINT",FACE,{"disambiguationData":[TD([[makeQuery(id+"F1.imprint","IMPRINT",EDGE,{"derivedFrom":subQ3}),1.0]])]});}
            extrude(context, id + "F19", {"entities" : qUnion([Q0]), "depth" : 25.4 * mm, "offsetDistance" : 25.4 * mm});
        }
        {
            var Q0;
            {var subQ0=sQuery(id+"F1.wireOp",EDGE,"E156");Q0=makeQuery(id+"F1.imprint","IMPRINT",FACE,{"disambiguationData":[TD([[makeQuery(id+"F1.imprint","IMPRINT",EDGE,{"derivedFrom":subQ0}),-1.0]])]});}
            var Q1;
            {var subQ1=sQuery(id+"F1.wireOp",EDGE,"E37");Q1=makeQuery(id+"F1.imprint","IMPRINT",FACE,{"disambiguationData":[TD([[makeQuery(id+"F1.imprint","IMPRINT",EDGE,{"derivedFrom":subQ1}),-1.0]])]});}
            extrude(context, id + "F20", {"entities" : qUnion([Q0, Q1]), "depth" : 25.4 * mm, "offsetDistance" : 25.4 * mm});
        }
        {
            var Q0;
            {var subQ3=sQuery(id+"F1.wireOp",EDGE,"E30");Q0=makeQuery(id+"F1.imprint","IMPRINT",FACE,{"disambiguationData":[TD([[makeQuery(id+"F1.imprint","IMPRINT",EDGE,{"derivedFrom":subQ3}),1.0]])]});}
            var Q1;
            {var subQ4=sQuery(id+"F1.wireOp",EDGE,"E32");Q1=makeQuery(id+"F1.imprint","IMPRINT",FACE,{"disambiguationData":[TD([[makeQuery(id+"F1.imprint","IMPRINT",EDGE,{"derivedFrom":subQ4}),1.0]])]});}
            var Q2;
            Q2=makeQuery(id+"F1.imprint","IMPRINT",FACE,{"disambiguationData":[TD([[makeQuery(id+"F1.imprint","IMPRINT",EDGE,{"derivedFrom":sQuery(id+"F1.wireOp",EDGE,"E25")}),1.0]])]});
            var Q3;
            {var subQ5=sQuery(id+"F1.wireOp",EDGE,"E23");Q3=makeQuery(id+"F1.imprint","IMPRINT",FACE,{"disambiguationData":[TD([[makeQuery(id+"F1.imprint","IMPRINT",EDGE,{"derivedFrom":subQ5}),1.0]])]});}
            var Q4;
            {var subQ3=sQuery(id+"F1.wireOp",EDGE,"E36");Q4=makeQuery(id+"F1.imprint","IMPRINT",FACE,{"disambiguationData":[TD([[makeQuery(id+"F1.imprint","IMPRINT",EDGE,{"derivedFrom":subQ3}),1.0]])]});}
            var Q5;
            Q5=makeQuery(id+"F1.imprint","IMPRINT",FACE,{"disambiguationData":[TD([[makeQuery(id+"F1.imprint","IMPRINT",EDGE,{"derivedFrom":sQuery(id+"F1.wireOp",EDGE,"E11")}),-1.0]])]});
            var Q6;
            {var subQ0=sQuery(id+"F1.wireOp",EDGE,"E149");Q6=makeQuery(id+"F1.imprint","IMPRINT",FACE,{"disambiguationData":[TD([[makeQuery(id+"F1.imprint","IMPRINT",EDGE,{"derivedFrom":subQ0}),-1.0]])]});}
            var Q7;
            {var subQ0=sQuery(id+"F1.wireOp",EDGE,"E150");Q7=makeQuery(id+"F1.imprint","IMPRINT",FACE,{"disambiguationData":[TD([[makeQuery(id+"F1.imprint","IMPRINT",EDGE,{"derivedFrom":subQ0}),-1.0]])]});}
            extrude(context, id + "F21", {"entities" : qUnion([Q0, Q1, Q2, Q3, Q4, Q5, Q6, Q7]), "depth" : 25.4 * mm, "offsetDistance" : 25.4 * mm});
        }
        {
            var Q0;
            {var subQ2=sQuery(id+"F1.wireOp",EDGE,"E178");Q0=makeQuery(id+"F1.imprint","IMPRINT",FACE,{"disambiguationData":[TD([[makeQuery(id+"F1.imprint","IMPRINT",EDGE,{"derivedFrom":subQ2}),-1.0]])]});}
            var Q1;
            {var subQ0=sQuery(id+"F1.wireOp",EDGE,"E176");Q1=makeQuery(id+"F1.imprint","IMPRINT",FACE,{"disambiguationData":[TD([[makeQuery(id+"F1.imprint","IMPRINT",EDGE,{"derivedFrom":subQ0}),-1.0]])]});}
            var Q2;
            {var subQ0=sQuery(id+"F1.wireOp",EDGE,"E133");var subQ1=sQuery(id+"F1.wireOp",EDGE,"E53");var subQ2=makeQuery(id+"F1.imprint","INTERSECT",VERTEX,{"derivedFrom":[subQ1,subQ0]});Q2=makeQuery(id+"F1.imprint","IMPRINT",FACE,{"disambiguationData":[TD([[makeQuery(id+"F1.imprint","IMPRINT",EDGE,{"disambiguationData":[TD([[subQ2,1.0]])],"derivedFrom":subQ1}),-1.0]])]});}
            extrude(context, id + "F22", {"entities" : qUnion([Q0, Q1, Q2]), "depth" : 25.4 * mm, "offsetDistance" : 25.4 * mm});
        }
        {
            var Q0;
            {var subQ0=sQuery(id+"F1.wireOp",EDGE,"E53");var subQ1=sQuery(id+"F1.wireOp",EDGE,"E52");var subQ2=makeQuery(id+"F1.imprint","INTERSECT",VERTEX,{"derivedFrom":[subQ1,subQ0]});Q0=makeQuery(id+"F1.imprint","IMPRINT",FACE,{"disambiguationData":[TD([[makeQuery(id+"F1.imprint","IMPRINT",EDGE,{"disambiguationData":[TD([[subQ2,1.0]])],"derivedFrom":subQ1}),-1.0]])]});}
            var Q1;
            {var subQ0=sQuery(id+"F1.wireOp",EDGE,"E179");Q1=makeQuery(id+"F1.imprint","IMPRINT",FACE,{"disambiguationData":[TD([[makeQuery(id+"F1.imprint","IMPRINT",EDGE,{"derivedFrom":subQ0}),1.0]])]});}
            var Q2;
            {var subQ3=sQuery(id+"F1.wireOp",EDGE,"E161");Q2=makeQuery(id+"F1.imprint","IMPRINT",FACE,{"disambiguationData":[TD([[makeQuery(id+"F1.imprint","IMPRINT",EDGE,{"derivedFrom":subQ3}),-1.0]])]});}
            var Q3;
            {var subQ3=sQuery(id+"F1.wireOp",EDGE,"E180");Q3=makeQuery(id+"F1.imprint","IMPRINT",FACE,{"disambiguationData":[TD([[makeQuery(id+"F1.imprint","IMPRINT",EDGE,{"derivedFrom":subQ3}),1.0]])]});}
            var Q4;
            {var subQ5=sQuery(id+"F1.wireOp",EDGE,"E181.trimOffspring");Q4=makeQuery(id+"F1.imprint","IMPRINT",FACE,{"disambiguationData":[TD([[makeQuery(id+"F1.imprint","IMPRINT",EDGE,{"derivedFrom":subQ5}),1.0]])]});}
            extrude(context, id + "F23", {"entities" : qUnion([Q0, Q1, Q2, Q3, Q4]), "depth" : 25.4 * mm, "offsetDistance" : 25.4 * mm});
        }
        {
            var Q0;
            {var subQ0=sQuery(id+"F1.wireOp",EDGE,"E160");Q0=makeQuery(id+"F1.imprint","IMPRINT",FACE,{"disambiguationData":[TD([[makeQuery(id+"F1.imprint","IMPRINT",EDGE,{"derivedFrom":subQ0}),1.0]])]});}
            var Q1;
            {var subQ0=sQuery(id+"F1.wireOp",EDGE,"E164.trimOffspring");Q1=makeQuery(id+"F1.imprint","IMPRINT",FACE,{"disambiguationData":[TD([[makeQuery(id+"F1.imprint","IMPRINT",EDGE,{"derivedFrom":subQ0}),1.0]])]});}
            extrude(context, id + "F24", {"entities" : qUnion([Q0, Q1]), "depth" : 25.4 * mm, "offsetDistance" : 25.4 * mm});
        }
        {
            var Q0;
            {var subQ0=sQuery(id+"F1.wireOp",EDGE,"E160");Q0=makeQuery(id+"F1.imprint","IMPRINT",FACE,{"disambiguationData":[TD([[makeQuery(id+"F1.imprint","IMPRINT",EDGE,{"derivedFrom":subQ0}),-1.0]])]});}
            var Q1;
            {var subQ0=sQuery(id+"F1.wireOp",EDGE,"E164.trimOffspring");Q1=makeQuery(id+"F1.imprint","IMPRINT",FACE,{"disambiguationData":[TD([[makeQuery(id+"F1.imprint","IMPRINT",EDGE,{"derivedFrom":subQ0}),-1.0]])]});}
            extrude(context, id + "F25", {"entities" : qUnion([Q0, Q1]), "depth" : 25.4 * mm, "offsetDistance" : 25.4 * mm});
        }
        {
            var Q0;
            {var subQ0=sQuery(id+"F1.wireOp",EDGE,"E165");Q0=makeQuery(id+"F1.imprint","IMPRINT",FACE,{"disambiguationData":[TD([[makeQuery(id+"F1.imprint","IMPRINT",EDGE,{"derivedFrom":subQ0}),-1.0]])]});}
            extrude(context, id + "F26", {"entities" : qUnion([Q0]), "depth" : 25.4 * mm, "offsetDistance" : 25.4 * mm});
        }
        {
            var Q0;
            {var subQ0=sQuery(id+"F1.wireOp",EDGE,"E169.trimOffspring");Q0=makeQuery(id+"F1.imprint","IMPRINT",FACE,{"disambiguationData":[TD([[makeQuery(id+"F1.imprint","IMPRINT",EDGE,{"derivedFrom":subQ0}),-1.0]])]});}
            var Q1;
            {var subQ0=sQuery(id+"F1.wireOp",EDGE,"E165");Q1=makeQuery(id+"F1.imprint","IMPRINT",FACE,{"disambiguationData":[TD([[makeQuery(id+"F1.imprint","IMPRINT",EDGE,{"derivedFrom":subQ0}),1.0]])]});}
            extrude(context, id + "F27", {"entities" : qUnion([Q0, Q1]), "depth" : 25.4 * mm, "offsetDistance" : 25.4 * mm});
        }
        {
            var Q0;
            {var subQ0=sQuery(id+"F1.wireOp",EDGE,"E134");Q0=makeQuery(id+"F1.imprint","IMPRINT",FACE,{"disambiguationData":[TD([[makeQuery(id+"F1.imprint","IMPRINT",EDGE,{"derivedFrom":subQ0}),-1.0]])]});}
            var Q1;
            Q1=makeQuery(id+"F1.imprint","IMPRINT",FACE,{"disambiguationData":[TD([[makeQuery(id+"F1.imprint","IMPRINT",EDGE,{"derivedFrom":sQuery(id+"F1.wireOp",EDGE,"E137")}),1.0]])]});
            var Q2;
            {var subQ0=sQuery(id+"F1.wireOp",EDGE,"E58.left");Q2=makeQuery(id+"F1.imprint","IMPRINT",FACE,{"disambiguationData":[TD([[makeQuery(id+"F1.imprint","IMPRINT",EDGE,{"derivedFrom":subQ0}),1.0]])]});}
            var Q3;
            {var subQ0=sQuery(id+"F1.wireOp",EDGE,"E58.top");Q3=makeQuery(id+"F1.imprint","IMPRINT",FACE,{"disambiguationData":[TD([[makeQuery(id+"F1.imprint","IMPRINT",EDGE,{"derivedFrom":subQ0}),1.0]])]});}
            extrude(context, id + "F28", {"entities" : qUnion([Q0, Q1, Q2, Q3]), "depth" : 25.4 * mm, "offsetDistance" : 25.4 * mm});
        }
        {
            var Q0;
            {var subQ0=sQuery(id+"F1.wireOp",EDGE,"E88");Q0=makeQuery(id+"F1.imprint","IMPRINT",FACE,{"disambiguationData":[TD([[makeQuery(id+"F1.imprint","IMPRINT",EDGE,{"derivedFrom":subQ0}),1.0]])]});}
            var Q1;
            {var subQ0=sQuery(id+"F1.wireOp",EDGE,"E91");Q1=makeQuery(id+"F1.imprint","IMPRINT",FACE,{"disambiguationData":[TD([[makeQuery(id+"F1.imprint","IMPRINT",EDGE,{"derivedFrom":subQ0}),1.0]])]});}
            extrude(context, id + "F29", {"entities" : qUnion([Q0, Q1]), "depth" : 25.4 * mm, "offsetDistance" : 25.4 * mm});
        }
        {
            var Q0;
            {var subQ0=sQuery(id+"F1.wireOp",EDGE,"E198");Q0=makeQuery(id+"F1.imprint","IMPRINT",FACE,{"disambiguationData":[TD([[makeQuery(id+"F1.imprint","IMPRINT",EDGE,{"derivedFrom":subQ0}),-1.0]])]});}
            extrude(context, id + "F30", {"entities" : qUnion([Q0]), "depth" : 25.4 * mm, "offsetDistance" : 25.4 * mm});
        }
        {
            var Q0;
            {var subQ3=sQuery(id+"F1.wireOp",EDGE,"E140");Q0=makeQuery(id+"F1.imprint","IMPRINT",FACE,{"disambiguationData":[TD([[makeQuery(id+"F1.imprint","IMPRINT",EDGE,{"derivedFrom":subQ3}),-1.0]])]});}
            extrude(context, id + "F31", {"entities" : qUnion([Q0]), "depth" : 25.4 * mm, "offsetDistance" : 25.4 * mm});
        }
        {
            var Q0;
            {var subQ0=sQuery(id+"F1.wireOp",EDGE,"E140");Q0=makeQuery(id+"F1.imprint","IMPRINT",FACE,{"disambiguationData":[TD([[makeQuery(id+"F1.imprint","IMPRINT",EDGE,{"derivedFrom":subQ0}),1.0]])]});}
            extrude(context, id + "F32", {"entities" : qUnion([Q0]), "depth" : 25.4 * mm, "offsetDistance" : 25.4 * mm});
        }
        {
            var Q0;
            Q0=qCreatedBy(makeId("Front.planeOp"),FACE);
            var sketch = newSketch(context, id + "F33", { "sketchPlane" : qUnion([Q0])});
            skLineSegment(sketch, "E201.0.0", {"start": v(139.06, -109.12) * mm, "end": v(139.06, -54.72) * mm});
            skLineSegment(sketch, "E201.0.1", {"start": v(139.06, -54.72) * mm, "end": v(139.06, 105.14) * mm});
            skLineSegment(sketch, "E201.0.2", {"start": v(139.06, 105.14) * mm, "end": v(-146.62, 105.14) * mm});
            skLineSegment(sketch, "E201.0.3", {"start": v(-146.62, 105.14) * mm, "end": v(-146.62, -109.12) * mm});
            skLineSegment(sketch, "E201.0.4", {"start": v(-146.62, -109.12) * mm, "end": v(139.06, -109.12) * mm});
            skPoint(sketch, "E202.0", {"position": v(-66.86, -16.48) * mm});
            skPoint(sketch, "E203.0", {"position": v(-49.11, -17.1) * mm});
            skPoint(sketch, "E204.0", {"position": v(-70.05, -16.47) * mm});
            skPoint(sketch, "E205.0", {"position": v(-46.2, -17.22) * mm});
            skPoint(sketch, "E206.0", {"position": v(-44.98, -16.42) * mm});
            skLineSegment(sketch, "E207.0", {"start": v(-60.38, -13.22) * mm, "end": v(-49.07, -13.33) * mm});
            skLineSegment(sketch, "E208.0", {"start": v(-60.38, -13.22) * mm, "end": v(-65.22, -13.17) * mm});
            skLineSegment(sketch, "E209.0", {"start": v(-65.22, 12.42) * mm, "end": v(-65.22, -15.22) * mm});
            skLineSegment(sketch, "E210.0", {"start": v(-48.8, 12.25) * mm, "end": v(-49.1, -16.67) * mm});
            skLineSegment(sketch, "E211", {"start": v(-49.1, -16.67) * mm, "end": v(-46.2, -16.7) * mm});
            skLineSegment(sketch, "E212", {"start": v(-46.2, -16.7) * mm, "end": v(-45, -15.71) * mm});
            skLineSegment(sketch, "E213", {"start": v(-45, -15.71) * mm, "end": v(-49.09, -19.1) * mm});
            skLineSegment(sketch, "E214", {"start": v(-49.95, -22.82) * mm, "end": v(-45, -18.71) * mm});
            skLineSegment(sketch, "E215", {"start": v(-45, -15.71) * mm, "end": v(-45, -18.71) * mm});
            skLineSegment(sketch, "E216", {"start": v(-49.95, -22.82) * mm, "end": v(-49.95, -21.01) * mm});
            skLineSegment(sketch, "E217", {"start": v(-49.95, -21.01) * mm, "end": v(-49.09, -20.3) * mm});
            skLineSegment(sketch, "E218", {"start": v(-49.09, -20.3) * mm, "end": v(-49.09, -19.1) * mm});
            skLineSegment(sketch, "E219", {"start": v(-49.09, -19.1) * mm, "end": v(-78.22, -18.8) * mm});
            skLineSegment(sketch, "E220", {"start": v(-49.09, -20.3) * mm, "end": v(-78.22, -20) * mm});
            skLineSegment(sketch, "E221", {"start": v(-49.95, -21.01) * mm, "end": v(-78.22, -20.72) * mm});
            skLineSegment(sketch, "E222", {"start": v(-49.95, -22.82) * mm, "end": v(-78.22, -22.53) * mm});
            skLineSegment(sketch, "E223", {"start": v(-70.05, -16.47) * mm, "end": v(-71.72, -17.7) * mm});
            skLineSegment(sketch, "E224", {"start": v(-49.95, -22.82) * mm, "end": v(-77.3, -45.5) * mm});
            skLineSegment(sketch, "E225", {"start": v(-107.38, -44.14) * mm, "end": v(-107.38, -41.4) * mm});
            skLineSegment(sketch, "E226.trimOffspring", {"start": v(-78.22, -22.53) * mm, "end": v(-107.38, -44.14) * mm});
            skLineSegment(sketch, "E227", {"start": v(-78.22, -22.53) * mm, "end": v(-78.22, -20.72) * mm});
            skLineSegment(sketch, "E228", {"start": v(-107.38, -41.4) * mm, "end": v(-78.22, -20.72) * mm});
            skLineSegment(sketch, "E229", {"start": v(-78.22, -20.72) * mm, "end": v(-78.74, -20) * mm});
            skLineSegment(sketch, "E230", {"start": v(-107.38, -41.4) * mm, "end": v(-111.18, -41.4) * mm});
            skLineSegment(sketch, "E231", {"start": v(-111.18, -41.4) * mm, "end": v(-78.74, -20) * mm});
            skLineSegment(sketch, "E232", {"start": v(-78.22, -20) * mm, "end": v(-78.74, -20) * mm});
            skLineSegment(sketch, "E233", {"start": v(-78.22, -18.8) * mm, "end": v(-78.74, -18.8) * mm});
            skLineSegment(sketch, "E234", {"start": v(-78.74, -20) * mm, "end": v(-78.74, -18.8) * mm});
            skLineSegment(sketch, "E235", {"start": v(-111.18, -41.4) * mm, "end": v(-111.18, -38.67) * mm});
            skLineSegment(sketch, "E236", {"start": v(-111.18, -38.67) * mm, "end": v(-78.74, -18.8) * mm});
            skLineSegment(sketch, "E237", {"start": v(-111.18, -38.67) * mm, "end": v(-146.62, -36.33) * mm});
            skLineSegment(sketch, "E238.0", {"start": v(-117.92, -11.06) * mm, "end": v(-133.04, -10.5) * mm});
            skLineSegment(sketch, "E239.0", {"start": v(-133.04, -14.77) * mm, "end": v(-133.04, 13.04) * mm});
            skLineSegment(sketch, "E240.0", {"start": v(-137.03, 20.59) * mm, "end": v(-137.03, -15.42) * mm});
            skLineSegment(sketch, "E241.0", {"start": v(-134.46, -15.51) * mm, "end": v(-137.03, -15.42) * mm});
            skLineSegment(sketch, "E242.0", {"start": v(-134.46, -15.51) * mm, "end": v(-133.04, -14.77) * mm});
            skLineSegment(sketch, "E243.0", {"start": v(-74.47, 12.64) * mm, "end": v(-74.59, -17.7) * mm});
            skLineSegment(sketch, "E244.0", {"start": v(-74.59, -17.7) * mm, "end": v(-71.72, -17.7) * mm});
            skLineSegment(sketch, "E245.0", {"start": v(-70.05, -16.47) * mm, "end": v(-66.86, -16.48) * mm});
            skLineSegment(sketch, "E246.trimOffspring", {"start": v(-137.03, -10.36) * mm, "end": v(-146.62, -10) * mm});
            skLineSegment(sketch, "E247", {"start": v(-107.38, -44.14) * mm, "end": v(-146.62, -42.37) * mm});
            skLineSegment(sketch, "E248", {"start": v(-107.38, -44.14) * mm, "end": v(-77.3, -45.5) * mm});
            skLineSegment(sketch, "E249", {"start": v(-146.62, -36.33) * mm, "end": v(-146.62, -42.37) * mm});
            skLineSegment(sketch, "E250.0", {"start": v(-74.57, -12.64) * mm, "end": v(-116.53, -11.1) * mm});
            skLineSegment(sketch, "E251.0.1", {"start": v(-71.72, -17.7) * mm, "end": v(-71.72, 20.3) * mm});
            skLineSegment(sketch, "E251.0.2", {"start": v(-71.72, 20.3) * mm, "end": v(-137.03, 20.59) * mm});
            skLineSegment(sketch, "E251.0.4", {"start": v(-137.03, -15.42) * mm, "end": v(-134.46, -15.51) * mm});
            skLineSegment(sketch, "E251.0.5", {"start": v(-134.46, -15.51) * mm, "end": v(-134.46, 13.05) * mm});
            skLineSegment(sketch, "E251.0.6", {"start": v(-134.46, 13.05) * mm, "end": v(-74.47, 12.64) * mm});
            skLineSegment(sketch, "E252", {"start": v(-146.62, -36.33) * mm, "end": v(-146.62, -10) * mm});
            skLineSegment(sketch, "E253", {"start": v(-137.03, -10.36) * mm, "end": v(-137.03, -15.42) * mm});
            skLineSegment(sketch, "E254", {"start": v(-133.04, -10.5) * mm, "end": v(-74.57, -12.64) * mm});
            skLineSegment(sketch, "E255", {"start": v(-66.86, -16.48) * mm, "end": v(-65.22, -15.22) * mm});
            skLineSegment(sketch, "E256", {"start": v(-65.22, -15.22) * mm, "end": v(-65.22, -13.17) * mm});
            skLineSegment(sketch, "E257", {"start": v(-65.22, -13.17) * mm, "end": v(-49.07, -13.33) * mm});
            skSolve(sketch);
        }
        {
            var Q0;
            Q0=makeQuery(id+"F33.imprint","IMPRINT",FACE,{"disambiguationData":[TD([[makeQuery(id+"F33.imprint","IMPRINT",EDGE,{"derivedFrom":sQuery(id+"F33.wireOp",EDGE,"E212")}),-1.0]])]});
            extrude(context, id + "F34", {"entities" : qUnion([Q0]), "depth" : 25.4 * mm, "offsetDistance" : 25.4 * mm});
        }
        {
            var Q0;
            Q0=makeQuery(id+"F33.imprint","IMPRINT",FACE,{"disambiguationData":[TD([[makeQuery(id+"F33.imprint","IMPRINT",EDGE,{"derivedFrom":sQuery(id+"F33.wireOp",EDGE,"E225")}),1.0]])]});
            var Q1;
            Q1=makeQuery(id+"F33.imprint","IMPRINT",FACE,{"disambiguationData":[TD([[makeQuery(id+"F33.imprint","IMPRINT",EDGE,{"derivedFrom":sQuery(id+"F33.wireOp",EDGE,"E213")}),1.0]])]});
            extrude(context, id + "F35", {"entities" : qUnion([Q0, Q1]), "depth" : 25.4 * mm, "offsetDistance" : 25.4 * mm});
        }
        {
            var Q0;
            Q0=makeQuery(id+"F33.imprint","IMPRINT",FACE,{"disambiguationData":[TD([[makeQuery(id+"F33.imprint","IMPRINT",EDGE,{"derivedFrom":sQuery(id+"F33.wireOp",EDGE,"E231")}),1.0]])]});
            var Q1;
            Q1=makeQuery(id+"F33.imprint","IMPRINT",FACE,{"disambiguationData":[TD([[makeQuery(id+"F33.imprint","IMPRINT",EDGE,{"derivedFrom":sQuery(id+"F33.wireOp",EDGE,"E225")}),-1.0]])]});
            extrude(context, id + "F36", {"entities" : qUnion([Q0, Q1]), "depth" : 25.4 * mm, "offsetDistance" : 25.4 * mm});
        }
        {
            var Q0;
            Q0=makeQuery(id+"F33.imprint","IMPRINT",FACE,{"disambiguationData":[TD([[makeQuery(id+"F33.imprint","IMPRINT",EDGE,{"derivedFrom":sQuery(id+"F33.wireOp",EDGE,"E216")}),1.0]])]});
            var Q1;
            Q1=makeQuery(id+"F33.imprint","IMPRINT",FACE,{"disambiguationData":[TD([[makeQuery(id+"F33.imprint","IMPRINT",EDGE,{"derivedFrom":sQuery(id+"F33.wireOp",EDGE,"E218")}),1.0]])]});
            extrude(context, id + "F37", {"entities" : qUnion([Q0, Q1]), "depth" : 25.4 * mm, "offsetDistance" : 25.4 * mm});
        }
        {
            var Q0;
            Q0=makeQuery(id+"F33.imprint","IMPRINT",FACE,{"disambiguationData":[TD([[makeQuery(id+"F33.imprint","IMPRINT",EDGE,{"derivedFrom":sQuery(id+"F33.wireOp",EDGE,"E228")}),1.0]])]});
            var Q1;
            Q1=makeQuery(id+"F33.imprint","IMPRINT",FACE,{"disambiguationData":[TD([[makeQuery(id+"F33.imprint","IMPRINT",EDGE,{"derivedFrom":sQuery(id+"F33.wireOp",EDGE,"E222")}),1.0]])]});
            extrude(context, id + "F38", {"entities" : qUnion([Q0, Q1]), "depth" : 25.4 * mm, "offsetDistance" : 25.4 * mm});
        }
        {
            var Q0;
            Q0=makeQuery(id+"F33.imprint","IMPRINT",FACE,{"disambiguationData":[TD([[makeQuery(id+"F33.imprint","IMPRINT",EDGE,{"derivedFrom":sQuery(id+"F33.wireOp",EDGE,"E217")}),1.0]])]});
            extrude(context, id + "F39", {"entities" : qUnion([Q0]), "depth" : 25.4 * mm, "offsetDistance" : 25.4 * mm});
        }
    });
